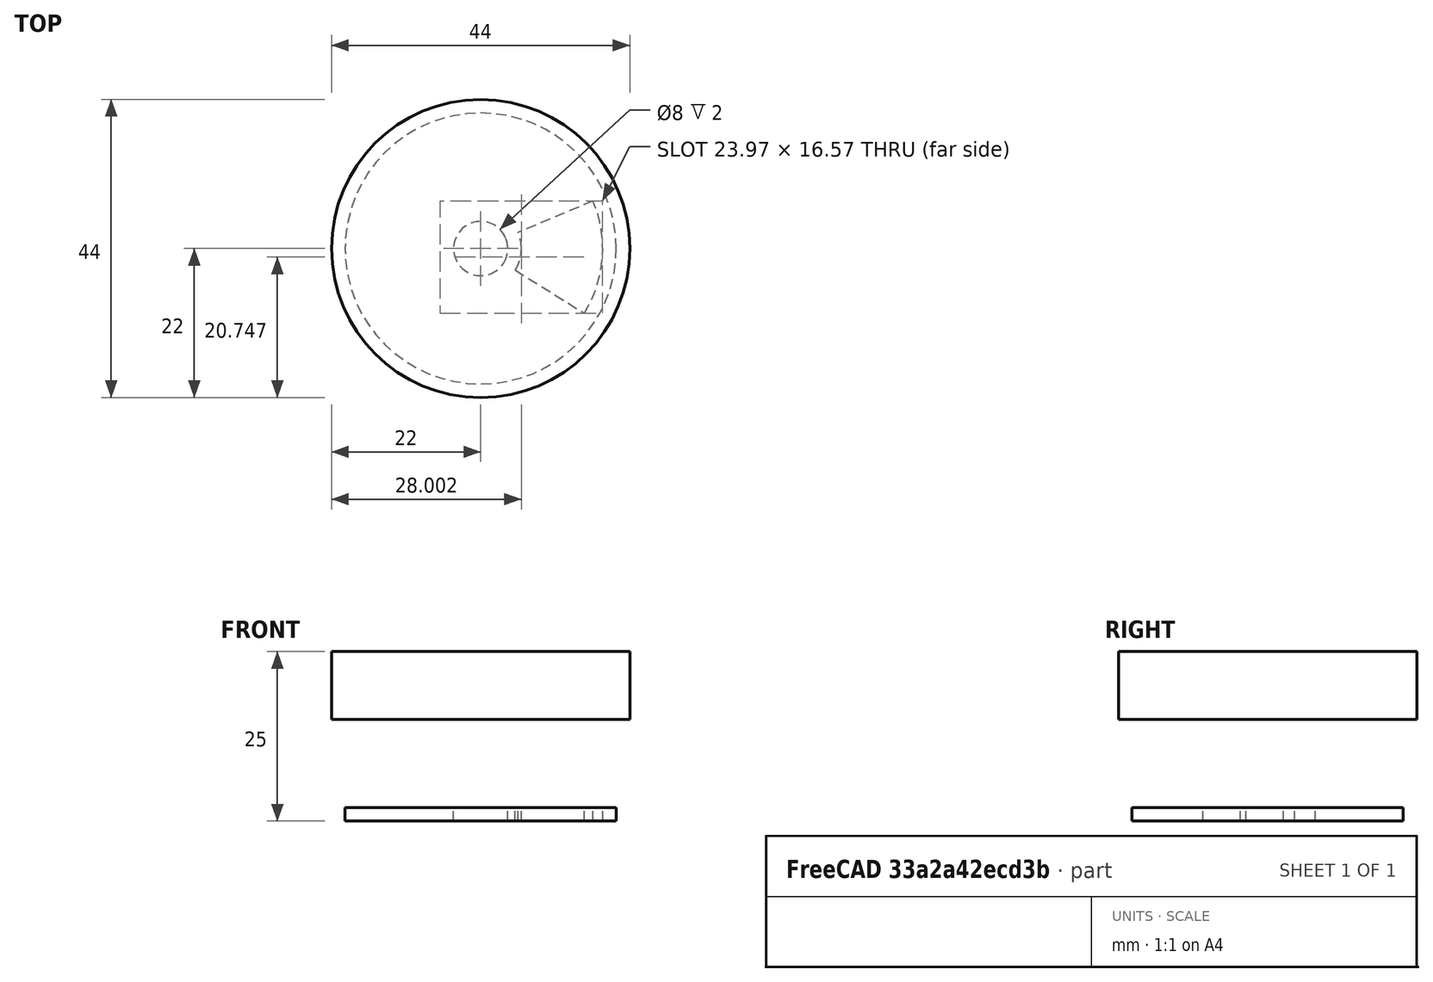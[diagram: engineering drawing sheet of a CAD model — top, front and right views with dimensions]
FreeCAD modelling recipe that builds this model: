
FCSTD DOCUMENT  (FreeCAD 0.14R3700 (Git))
Label: trampillasalidainferiordepastillav1
License: CC-BY 3.0
LicenseURL: http://creativecommons.org/licenses/by/3.0/
objects: Part::Cylinder×4, Part::Cut×2, Part::MultiCommon×1, Part::MultiFuse×1
note: 8 computed .brp shape members not serialized (recipe doc carries the construction recipe); baked Part::Feature solids carry a one-line shape summary decoded from their .brp

FEATURE [Part::Cylinder] Cylinder
  Angle = 360
  Height = 2
  Radius = 20
FEATURE [Part::Cylinder] Cylinder002
  Angle = 360
  Height = 2
  Radius = 6
FEATURE [Part::Cylinder] Cylinder003
  Angle = 360
  Height = 2
  Radius = 4
FEATURE [Part::MultiCommon] Common004
  Placement = pos=(0,0,2) rot=(0,0,-1;1.67552rad)
FEATURE [Part::Cylinder] Cylinder004
  Angle = 360
  Height = 10
  Placement = pos=(0,0,15) rot=(0,0,1;0rad)
  Radius = 22
FEATURE [Part::Cut] Cut
  Base = -> Cylinder
  Tool = -> Common004
FEATURE [Part::MultiFuse] Fusion
  Shapes = -> [Cylinder002,Cut]
FEATURE [Part::Cut] Cut001
  Base = -> Fusion
  Tool = -> Cylinder003
